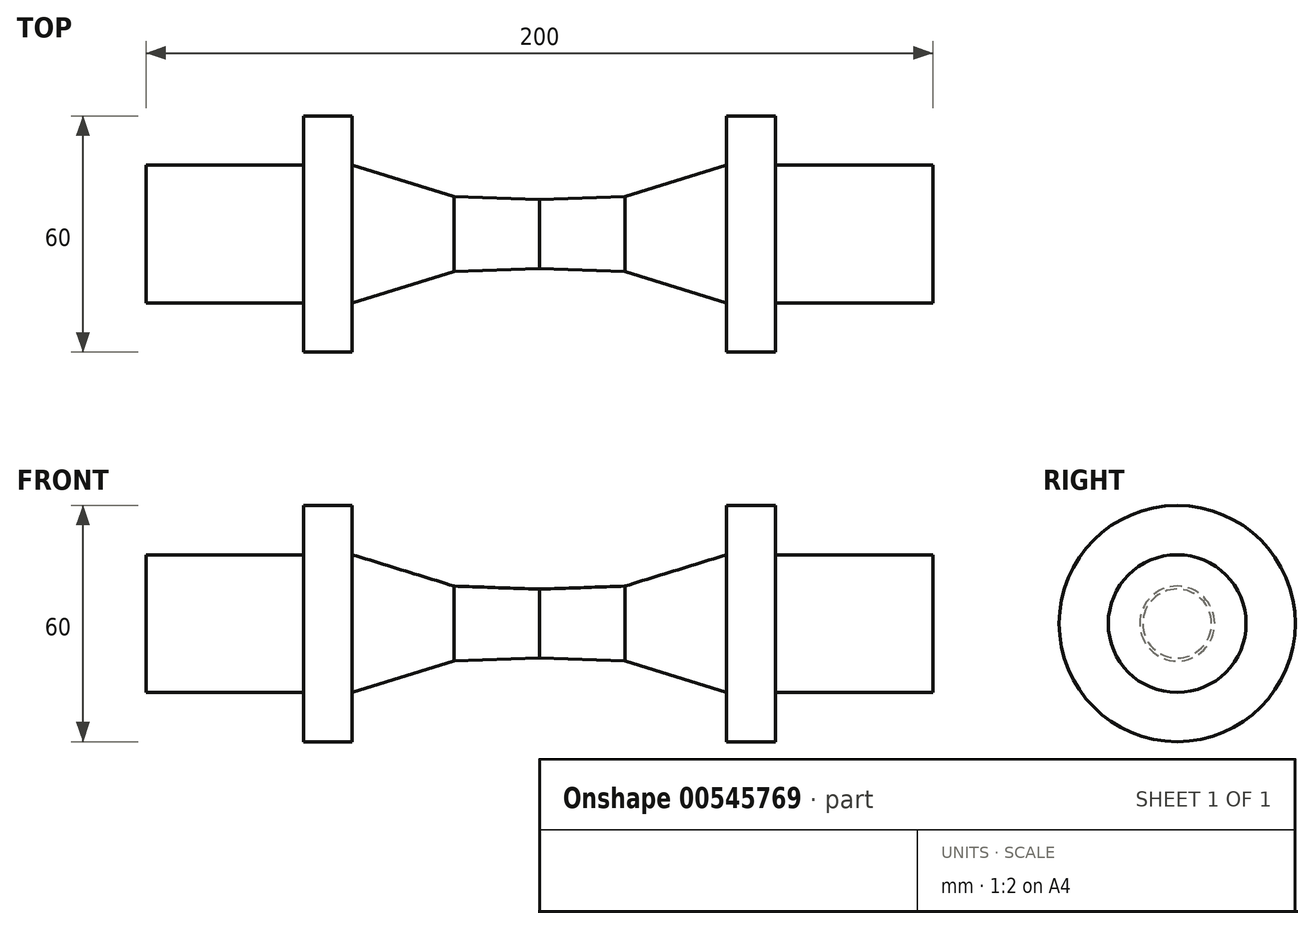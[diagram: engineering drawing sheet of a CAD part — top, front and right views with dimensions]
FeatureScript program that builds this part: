
annotation { "Feature Type Name" : "Feature", "Feature Type Description" : "" }
export const myFeature = defineFeature(function(context is Context, id is Id, definition is map)
    precondition{}
    {
        {
            var Q0;
            Q0=qCreatedBy(makeId("Front.planeOp"),FACE);
            var sketch = newSketch(context, id + "F0", { "sketchPlane" : qUnion([Q0])});
            skLineSegment(sketch, "E0", {"start": v(47.56, 17.5) * mm, "end": v(47.56, 30) * mm});
            skLineSegment(sketch, "E1", {"start": v(60, 30) * mm, "end": v(47.56, 30) * mm});
            skLineSegment(sketch, "E2", {"start": v(60, 30) * mm, "end": v(60, 17.5) * mm});
            skLineSegment(sketch, "E3", {"start": v(60, 17.5) * mm, "end": v(100, 17.5) * mm});
            skLineSegment(sketch, "E4", {"start": v(100, 17.5) * mm, "end": v(100, 0) * mm});
            skLineSegment(sketch, "E5", {"start": v(0, 0) * mm, "end": v(100, 0) * mm});
            skLineSegment(sketch, "E6", {"start": v(0, 0) * mm, "end": v(0, 17.5) * mm});
            skFitSpline(sketch, "E7", {"points": [v(21.68, 9.52) * mm, v(0, 8.75) * mm], "startDerivative": vector(-21.68, -0.77) * mm, "endDerivative": vector(-21.68, -0.77) * mm});
            skFitSpline(sketch, "E8", {"points": [v(1.59, 9.52) * mm, v(21.68, 9.52) * mm], "startDerivative": vector(20.1, 0) * mm, "endDerivative": vector(20.1, 0) * mm});
            skFitSpline(sketch, "E9", {"points": [v(21.68, 9.52) * mm, v(47.56, 17.5) * mm], "startDerivative": vector(25.88, 7.98) * mm, "endDerivative": vector(25.88, 7.98) * mm});
            skSolve(sketch);
        }
        {
            var Q0;
            Q0=makeQuery(id+"F0.imprint","IMPRINT",FACE,{"disambiguationData":[TD([[makeQuery(id+"F0.imprint","IMPRINT",EDGE,{"derivedFrom":sQuery(id+"F0.wireOp",EDGE,"E0")}),-1.0]])]});
            var Q1;
            Q1=sQuery(id+"F0.wireOp",EDGE,"E5");
            revolve(context, id + "F1", {"entities" : qUnion([Q0]), "axis" : qUnion([Q1]), "revolveType" : RevolveType.FULL});
        }
        {
            var Q0;
            Q0=makeQuery(id+"F1.opRevolve","SWEPT_BODY",BODY,{"disambiguationData":[OSD([sQuery(id+"F0.wireOp",EDGE,"E0"),sQuery(id+"F0.wireOp",EDGE,"E1"),sQuery(id+"F0.wireOp",EDGE,"E2"),sQuery(id+"F0.wireOp",EDGE,"E3"),sQuery(id+"F0.wireOp",EDGE,"E4"),sQuery(id+"F0.wireOp",EDGE,"E5"),sQuery(id+"F0.wireOp",EDGE,"E6"),sQuery(id+"F0.wireOp",EDGE,"E7"),sQuery(id+"F0.wireOp",EDGE,"E9")])]});
            var Q1;
            Q1=makeQuery(id+"F1.opRevolve","SWEPT_FACE",FACE,{"disambiguationData":[OSD([sQuery(id+"F0.wireOp",EDGE,"E6")])]});
            mirror(context, id + "F2", {"operationType" : NewBodyOperationType.ADD, "entities" : qUnion([Q0]), "mirrorPlane" : qUnion([Q1])});
        }
    });
